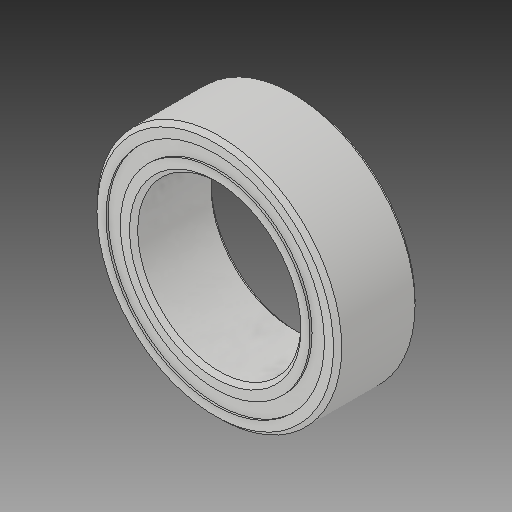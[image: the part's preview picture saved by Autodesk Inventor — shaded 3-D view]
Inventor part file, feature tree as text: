
AUTODESK INVENTOR PART (.ipt)
format: ipt  version: 2017 (Build 210142000, 142)  size: 604,672 bytes
history: native  units: in
note: dims shown in document units (in); Inventor stores cm internally (conversion verified against a paired STEP export)
features: other x11, revolve x5
ambient origin geometry x8: Origin, YZ Plane, XZ Plane, XY Plane, X Axis, Y Axis, Z Axis, Center Point
bodies: Solid1 (feature_tree), Solid2 (feature_tree), Solid3 (feature_tree), Solid4 (feature_tree), Solid5 (feature_tree), Solid6 (feature_tree), Solid7 (feature_tree), Solid8 (feature_tree), Solid9 (feature_tree), Solid10 (feature_tree), Solid11 (feature_tree), Solid12 (feature_tree), Solid13 (feature_tree), Solid14 (feature_tree), Solid15 (feature_tree), Solid16 (feature_tree)
feature tree (16):
  revolve  "Revolve1"  [1 undecoded]
  revolve  "Revolve3"  [1 undecoded]
  revolve  "Revolve4"  [1 undecoded]
  other  "CirPattern1[1]"
  other  "CirPattern1[2]"
  other  "CirPattern1[3]"
  other  "CirPattern1[4]"
  other  "CirPattern1[5]"
  other  "CirPattern1[6]"
  other  "CirPattern1[7]"
  other  "CirPattern1[8]"
  other  "CirPattern1[9]"
  other  "CirPattern1[10]"
  other  "CirPattern1[11]"
  revolve  "Revolve5[1]"  [1 undecoded]
  revolve  "Revolve5[2]"  [1 undecoded]
note: 5 required parameter values undecoded (feature->parameter linkage not recoverable at this tier; creation-order binding heuristic only, values carry confidence <= 0.55)
